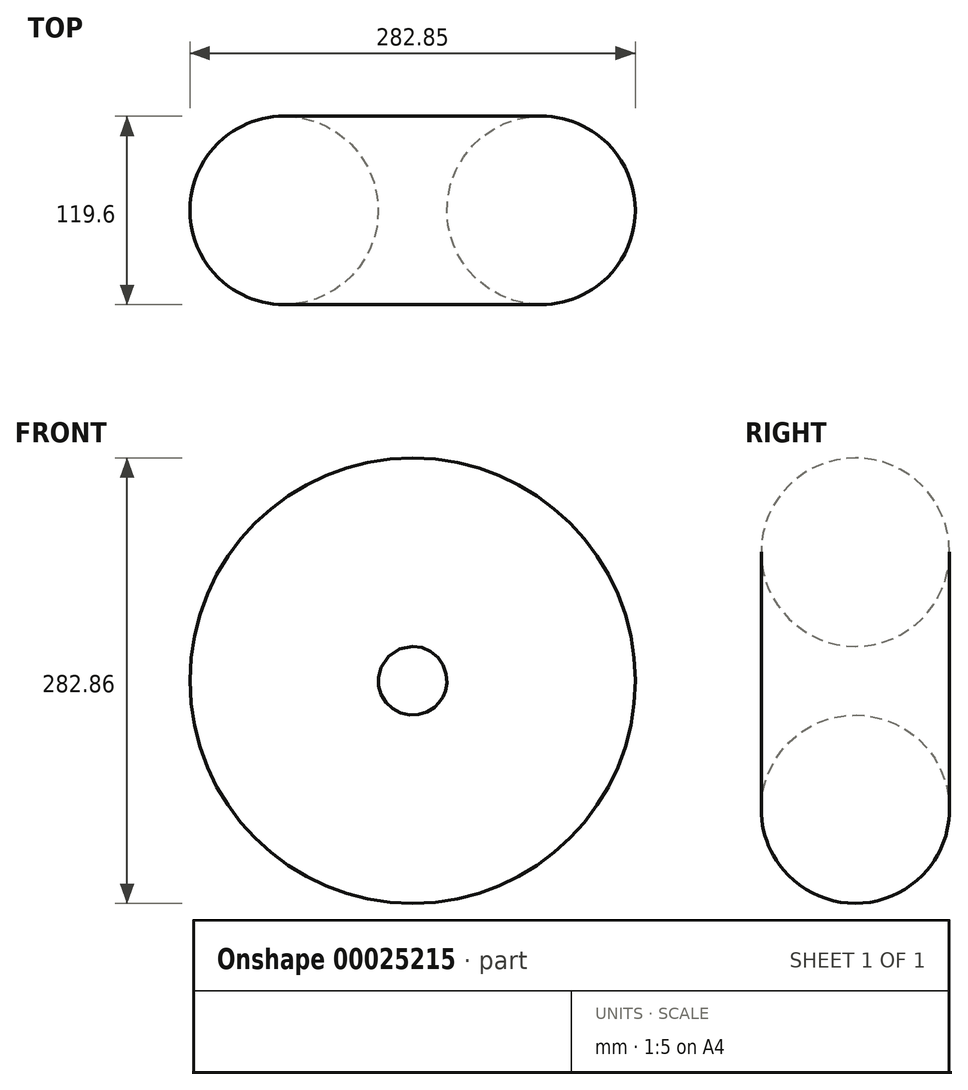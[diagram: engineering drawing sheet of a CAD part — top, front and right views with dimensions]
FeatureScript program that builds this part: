
annotation { "Feature Type Name" : "Feature", "Feature Type Description" : "" }
export const myFeature = defineFeature(function(context is Context, id is Id, definition is map)
    precondition{}
    {
        {
            var Q0;
            Q0=qCreatedBy(makeId("Top.planeOp"),FACE);
            var sketch = newSketch(context, id + "F0", { "sketchPlane" : qUnion([Q0])});
            skLineSegment(sketch, "E0", {"start": v(-81.62, 64.13) * mm, "end": v(-81.62, -59.42) * mm});
            skCircle(sketch, "E1", {"center": v(0, 0) * mm, "radius": 59.8 * mm});
            skSolve(sketch);
        }
        {
            var Q0;
            Q0=makeQuery(id+"F0.imprint","IMPRINT",FACE,{"disambiguationData":[TD([[makeQuery(id+"F0.imprint","IMPRINT",EDGE,{"derivedFrom":sQuery(id+"F0.wireOp",EDGE,"E1")}),1.0]])]});
            var Q1;
            Q1=sQuery(id+"F0.wireOp",EDGE,"E0");
            revolve(context, id + "F1", {"entities" : qUnion([Q0]), "axis" : qUnion([Q1]), "revolveType" : RevolveType.FULL});
        }
    });
